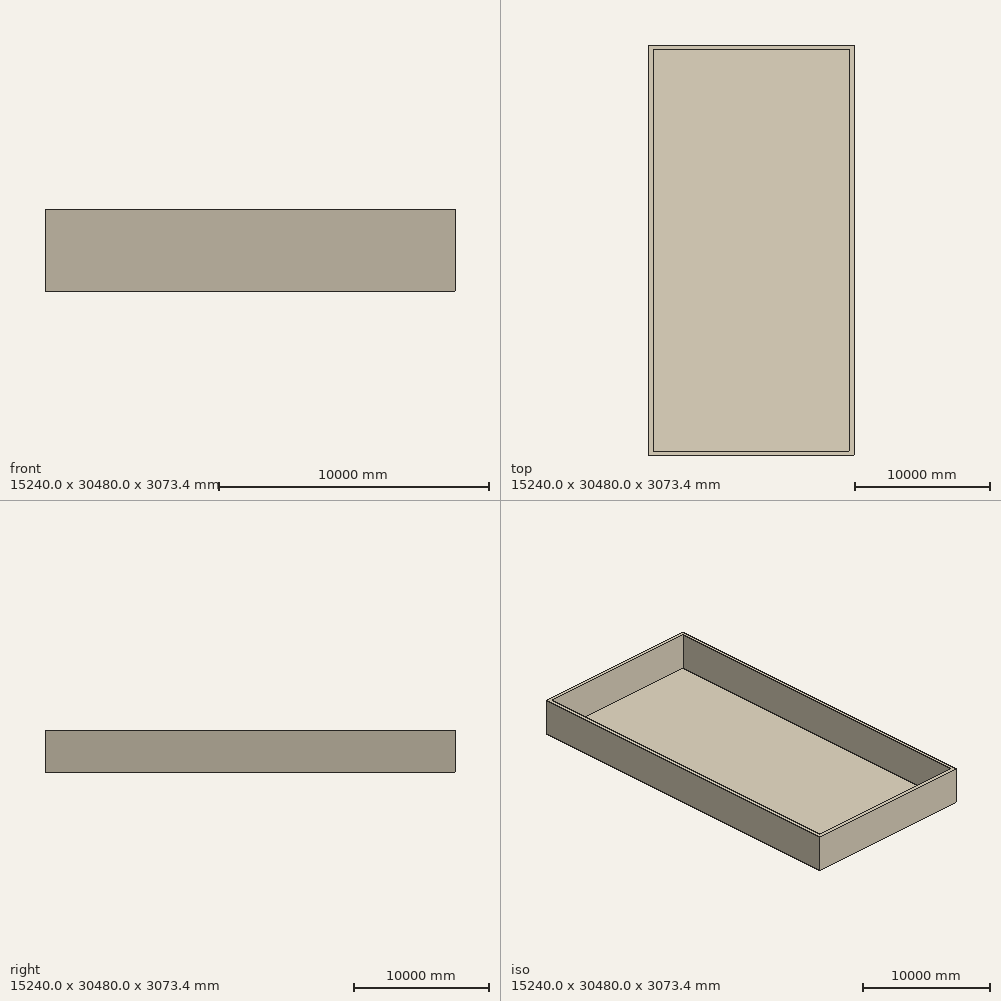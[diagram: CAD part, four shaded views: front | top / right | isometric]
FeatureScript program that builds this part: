
annotation { "Feature Type Name" : "Feature", "Feature Type Description" : "" }
export const myFeature = defineFeature(function(context is Context, id is Id, definition is map)
    precondition{}
    {
        {
            var Q0;
            Q0=qCreatedBy(makeId("Top.planeOp"),FACE);
            var sketch = newSketch(context, id + "F0", { "sketchPlane" : qUnion([Q0])});
            skLineSegment(sketch, "E0.bottom", {"start": v(0, 0) * mm, "end": v(15240, 0) * mm});
            skLineSegment(sketch, "E0.top", {"start": v(0, 30480) * mm, "end": v(15240, 30480) * mm});
            skLineSegment(sketch, "E0.left", {"start": v(0, 0) * mm, "end": v(0, 30480) * mm});
            skLineSegment(sketch, "E0.right", {"start": v(15240, 0) * mm, "end": v(15240, 30480) * mm});
            skPoint(sketch, "E0.middle", {"position": v(7620, 15240) * mm});
            skLineSegment(sketch, "E1.0", {"start": v(14935.2, 304.8) * mm, "end": v(14935.2, 30175.2) * mm});
            skLineSegment(sketch, "E1.1", {"start": v(304.8, 304.8) * mm, "end": v(14935.2, 304.8) * mm});
            skLineSegment(sketch, "E1.2", {"start": v(304.8, 304.8) * mm, "end": v(304.8, 30175.2) * mm});
            skLineSegment(sketch, "E1.3", {"start": v(304.8, 30175.2) * mm, "end": v(14935.2, 30175.2) * mm});
            skSolve(sketch);
        }
        {
            var Q0;
            Q0 = qSketchRegion(id + "F0", true);
            extrude(context, id + "F1", {"entities" : qUnion([Q0]), "depth" : 3048 * mm, "offsetDistance" : 25.4 * mm});
        }
        {
            var Q0;
            Q0=makeQuery(id+"F1.opExtrude","CAP_FACE",FACE,{"disambiguationData":[OSD([sQuery(id+"F0.wireOp",EDGE,"E0.bottom"),sQuery(id+"F0.wireOp",EDGE,"E0.top"),sQuery(id+"F0.wireOp",EDGE,"E0.left"),sQuery(id+"F0.wireOp",EDGE,"E0.right"),sQuery(id+"F0.wireOp",EDGE,"E1.0"),sQuery(id+"F0.wireOp",EDGE,"E1.1"),sQuery(id+"F0.wireOp",EDGE,"E1.2"),sQuery(id+"F0.wireOp",EDGE,"E1.3")])],"isStart":true});
            var sketch = newSketch(context, id + "F2", { "sketchPlane" : qUnion([Q0])});
            skLineSegment(sketch, "E2.0", {"start": v(0, 0) * mm, "end": v(15240, 0) * mm});
            skLineSegment(sketch, "E3.0", {"start": v(0, 0) * mm, "end": v(0, -30480) * mm});
            skLineSegment(sketch, "E4.0", {"start": v(15240, 0) * mm, "end": v(15240, -30480) * mm});
            skLineSegment(sketch, "E5.0", {"start": v(0, -30480) * mm, "end": v(15240, -30480) * mm});
            skSolve(sketch);
        }
        {
            var Q0;
            Q0 = qSketchRegion(id + "F2", true);
            extrude(context, id + "F3", {"entities" : qUnion([Q0]), "operationType" : NewBodyOperationType.ADD, "depth" : 25.4 * mm, "offsetDistance" : 25.4 * mm});
        }
    });
